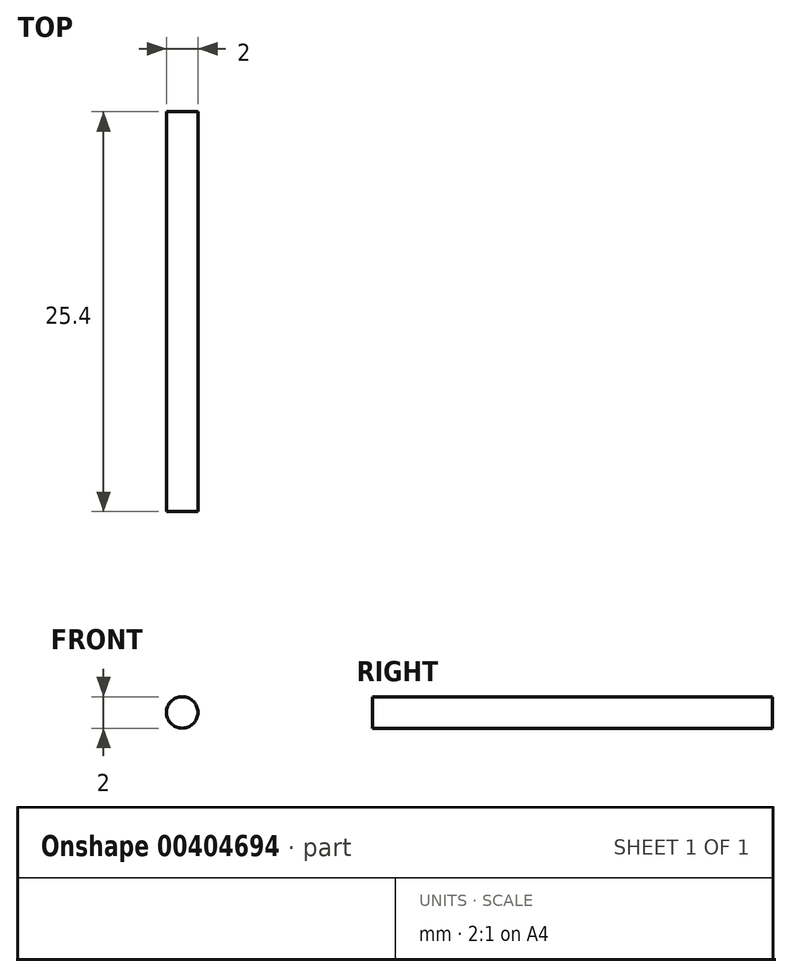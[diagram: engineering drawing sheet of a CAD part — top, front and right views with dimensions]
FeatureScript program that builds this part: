
annotation { "Feature Type Name" : "Feature", "Feature Type Description" : "" }
export const myFeature = defineFeature(function(context is Context, id is Id, definition is map)
    precondition{}
    {
        {
            var Q0;
            Q0=qCreatedBy(makeId("Front.planeOp"),FACE);
            var sketch = newSketch(context, id + "F0", { "sketchPlane" : qUnion([Q0])});
            skCircle(sketch, "E0", {"center": v(0, 0) * mm, "radius": 1 * mm});
            skSolve(sketch);
        }
        {
            var Q0;
            Q0 = qSketchRegion(id + "F0", true);
            extrude(context, id + "F1", {"entities" : qUnion([Q0]), "depth" : 25.4 * mm, "symmetric" : true});
        }
    });
